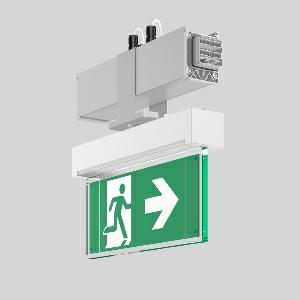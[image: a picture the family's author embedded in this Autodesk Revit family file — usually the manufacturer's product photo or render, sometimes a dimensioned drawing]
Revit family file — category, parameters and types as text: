
# Revit family: linedo_module_rz_9503rz_760_434_023_ed5e
name_source: partatom
category: Lighting Fixtures
units: mm (PartAtom-declared; Revit-internal decimal feet)

## family parameters
Cut with Voids When Loaded = No
Host = Face
Light Source = No
Part Type = Normal
Room Calculation Point = No
Round Connector Dimension = Use Diameter
Shared = No

## types (1)
- LINEDO Module RZ
    Apparent Load = 0 VA
    Default Elevation = 1800 mm
    Description = LINEDO, silver, on/off
Continuous line luminaire, L 336 B 62 H 308, SBS, 3 h, MultiDigit
    Height = 308 mm
    Lamp = 0 x
    Length = 336 mm
    Luminous efficacy = 0 lm/W
    Manufacturer = RZB
    ModVariant = No
    Model = 9503RZ.760.434.023
    Mounting Place = Ceiling
    Mounting Type = Surface mounted
    Number of Poles = 1
    OnlyDefault = Yes
    Power Factor = 1
    Product Name = LINEDO Module RZ
    Product group = Continuous line luminaire system Linedo IP 54
    ProductGroupID = 314
    Protection Class = Protection class I
    Protection Degree = IP 54
    RLX_Detail_Level = 1
    RLX_Emergency_Light_Flux = 0 lm
    RLX_Emergency_Type = 0
    RLX_Emergency_Type_DB = No
    RlxData = <blob elided: 34773 chars, md5=a675275a>
    Standby Power = 0 W
    System Light Flux = 0 lm
    System Power = 0 W
    Type Comments = Product without accessories
    Type Image = 9503rz.760.434.023.jpg
    URL = http://relux.com
    VarID = ---
    Voltage = 0 V
    Weight = 0.00 kg
    Width = 62 mm  [stored 0.203412 ft]

note: [stored X ft] marks values corroborated as IEEE doubles in the binary element streams (Revit-internal decimal feet)

## geometry (parser evidence)
native form markers: Blend x4, Sweep x12
no freeform markers — native parametric forms only
